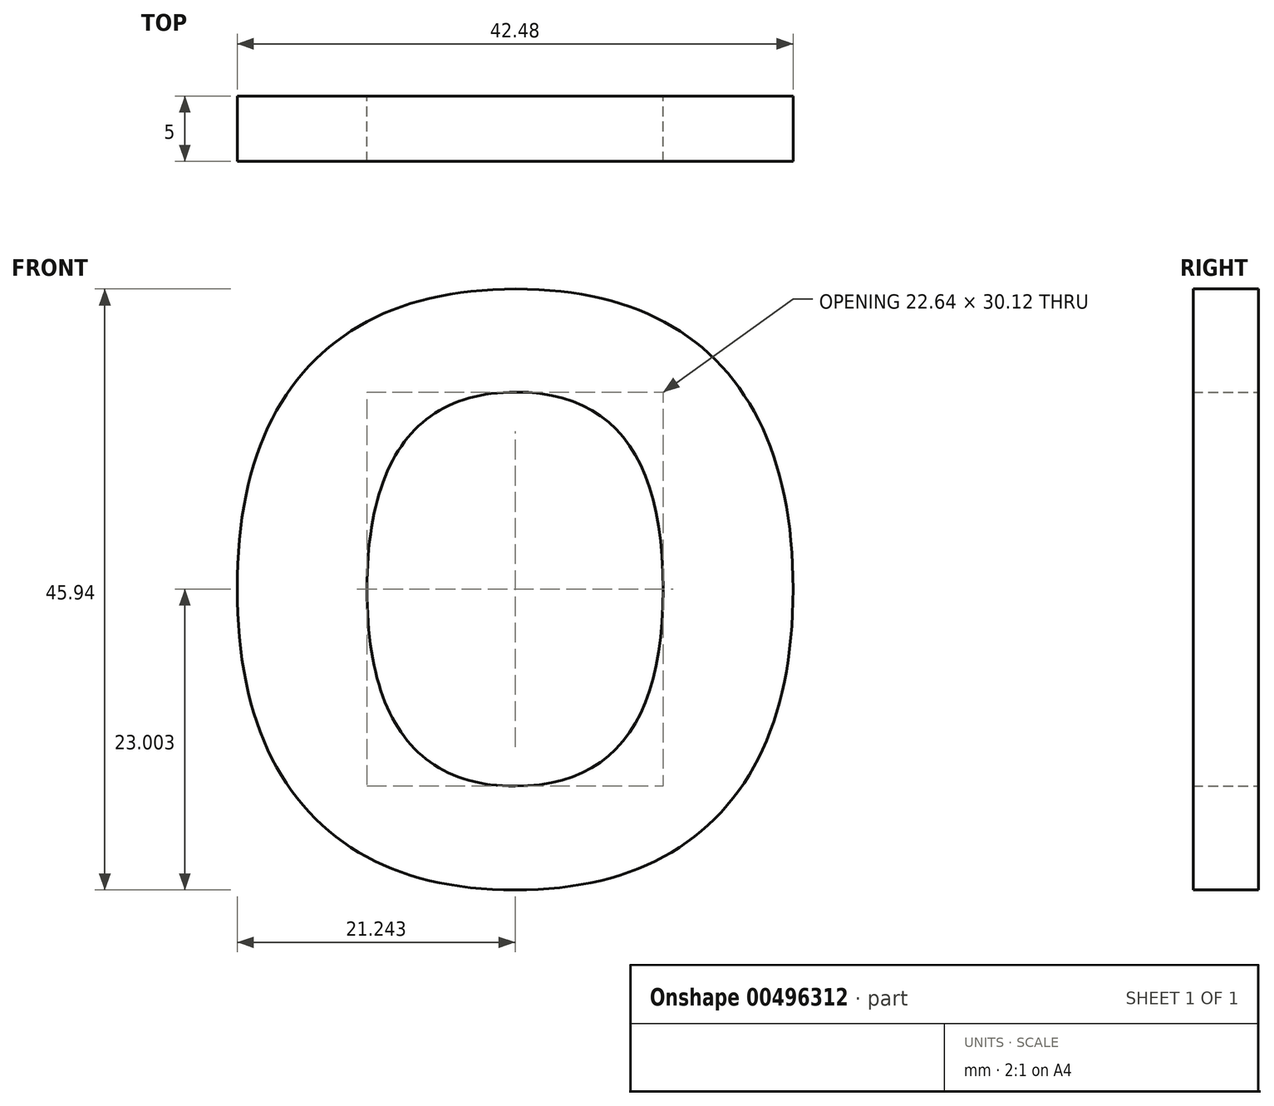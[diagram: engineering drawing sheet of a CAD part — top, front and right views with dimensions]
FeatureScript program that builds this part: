
annotation { "Feature Type Name" : "Feature", "Feature Type Description" : "" }
export const myFeature = defineFeature(function(context is Context, id is Id, definition is map)
    precondition{}
    {
        {
            var Q0;
            Q0=qCreatedBy(makeId("Front.planeOp"),FACE);
            var sketch = newSketch(context, id + "F0", { "sketchPlane" : qUnion([Q0])});
            skText(sketch, "E0", { "text": "O", "fontName": "OpenSans-Bold.ttf"});
            const initialGuessF0  = {"E0": [-0.0615, 0.00807, 1, 0, 0.045]};
            skSetInitialGuess(sketch, initialGuessF0);
            skSolve(sketch);
        }
        {
            var Q0;
            Q0=makeQuery(id+"F0.imprint","IMPRINT",FACE,{"disambiguationData":[TD([[makeQuery(id+"F0.imprint","IMPRINT",EDGE,{"derivedFrom":sQuery(id+"F0.wireOp",EDGE,"E0.sketch_text.stroke-0")}),-1.0]])]});
            extrude(context, id + "F1", {"entities" : qUnion([Q0]), "depth" : 5 * mm});
        }
    });
